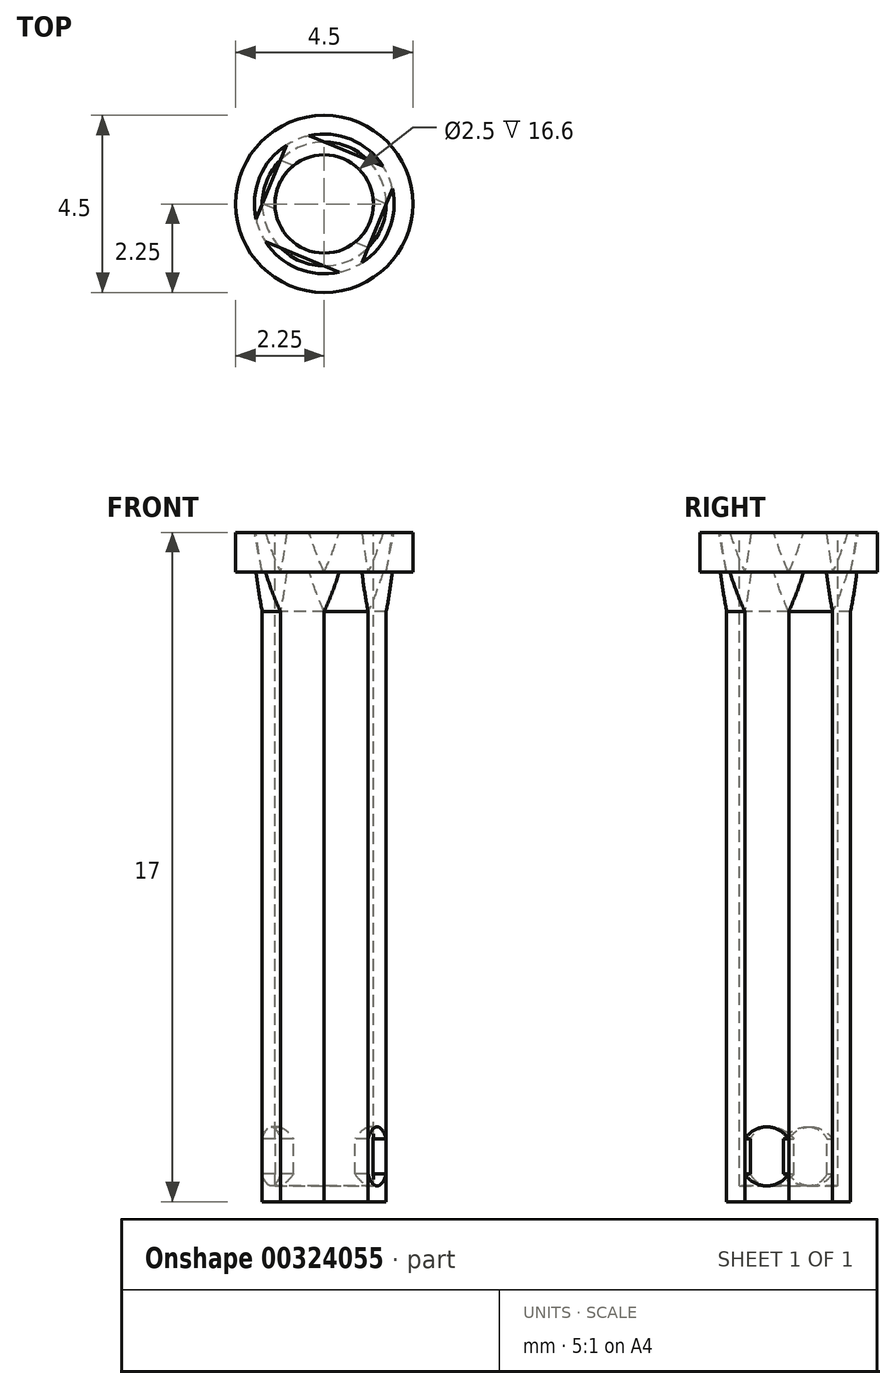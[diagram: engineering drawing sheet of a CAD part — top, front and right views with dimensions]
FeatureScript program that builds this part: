
annotation { "Feature Type Name" : "Feature", "Feature Type Description" : "" }
export const myFeature = defineFeature(function(context is Context, id is Id, definition is map)
    precondition{}
    {
        {
            var Q0;
            Q0=qCreatedBy(makeId("Front.planeOp"),FACE);
            var sketch = newSketch(context, id + "F0", { "sketchPlane" : qUnion([Q0])});
            skLineSegment(sketch, "E0.bottom", {"start": v(0, 0) * mm, "end": v(-1.58, 0) * mm});
            skLineSegment(sketch, "E0.top", {"start": v(0, 17) * mm, "end": v(-1.58, 17) * mm});
            skLineSegment(sketch, "E0.left", {"start": v(0, 0) * mm, "end": v(0, 17) * mm});
            skLineSegment(sketch, "E0.right", {"start": v(-1.58, 0) * mm, "end": v(-1.58, 17) * mm});
            skLineSegment(sketch, "E1.bottom", {"start": v(-1.58, 17) * mm, "end": v(-2.25, 17) * mm});
            skLineSegment(sketch, "E1.top", {"start": v(-1.58, 16) * mm, "end": v(-2.25, 16) * mm});
            skLineSegment(sketch, "E1.left", {"start": v(-1.58, 17) * mm, "end": v(-1.58, 16) * mm});
            skLineSegment(sketch, "E1.right", {"start": v(-2.25, 17) * mm, "end": v(-2.25, 16) * mm});
            skLineSegment(sketch, "E2.bottom", {"start": v(-1.25, 17) * mm, "end": v(0, 17) * mm});
            skLineSegment(sketch, "E2.top", {"start": v(-1.25, 0.4) * mm, "end": v(0, 0.4) * mm});
            skLineSegment(sketch, "E2.left", {"start": v(-1.25, 17) * mm, "end": v(-1.25, 0.4) * mm});
            skLineSegment(sketch, "E2.right", {"start": v(0, 17) * mm, "end": v(0, 0.4) * mm});
            skSolve(sketch);
        }
        {
            var Q0;
            Q0=makeQuery(id+"F0.imprint","IMPRINT",FACE,{"disambiguationData":[TD([[makeQuery(id+"F0.imprint","IMPRINT",EDGE,{"derivedFrom":sQuery(id+"F0.wireOp",EDGE,"E0.bottom")}),-1.0]])]});
            var Q1;
            Q1=makeQuery(id+"F0.imprint","IMPRINT",FACE,{"disambiguationData":[TD([[makeQuery(id+"F0.imprint","IMPRINT",EDGE,{"derivedFrom":sQuery(id+"F0.wireOp",EDGE,"E1.bottom")}),1.0]])]});
            var Q2;
            Q2=sQuery(id+"F0.wireOp",EDGE,"E2.right");
            revolve(context, id + "F1", {"entities" : qUnion([Q0, Q1]), "axis" : qUnion([Q2]), "revolveType" : RevolveType.FULL});
        }
        {
            var Q0;
            Q0=makeQuery(id+"F1.opRevolve","SWEPT_FACE",FACE,{"disambiguationData":[OSD([sQuery(id+"F0.wireOp",EDGE,"E0.bottom")])]});
            var sketch = newSketch(context, id + "F2", { "sketchPlane" : qUnion([Q0])});
            skCircle(sketch, "E3.cCircle", {"center": v(0, 0) * mm, "radius": 1.46 * mm, "construction": true});
            skLineSegment(sketch, "E3.0", {"start": v(1.11, -1.11) * mm, "end": v(0, -1.58) * mm});
            skLineSegment(sketch, "E3.1", {"start": v(0, -1.58) * mm, "end": v(-1.11, -1.11) * mm});
            skLineSegment(sketch, "E3.2", {"start": v(-1.11, -1.11) * mm, "end": v(-1.58, 0) * mm});
            skLineSegment(sketch, "E3.3", {"start": v(-1.58, 0) * mm, "end": v(-1.11, 1.11) * mm});
            skLineSegment(sketch, "E3.4", {"start": v(-1.11, 1.11) * mm, "end": v(0, 1.58) * mm});
            skLineSegment(sketch, "E3.5", {"start": v(0, 1.58) * mm, "end": v(1.11, 1.11) * mm});
            skLineSegment(sketch, "E3.6", {"start": v(1.11, 1.11) * mm, "end": v(1.58, 0) * mm});
            skLineSegment(sketch, "E3.7", {"start": v(1.58, 0) * mm, "end": v(1.11, -1.11) * mm});
            skPoint(sketch, "E3.0.midPoint", {"position": v(0.56, -1.34) * mm});
            skCircle(sketch, "E4", {"center": v(0, 0) * mm, "radius": 1.58 * mm});
            skSolve(sketch);
        }
        {
            var Q0;
            {var subQ0=sQuery(id+"F2.wireOp",EDGE,"E3.2");Q0=makeQuery(id+"F2.imprint","IMPRINT",FACE,{"disambiguationData":[TD([[makeQuery(id+"F2.imprint","IMPRINT",EDGE,{"derivedFrom":subQ0}),1.0]])]});}
            var Q1;
            {var subQ0=sQuery(id+"F2.wireOp",EDGE,"E3.4");Q1=makeQuery(id+"F2.imprint","IMPRINT",FACE,{"disambiguationData":[TD([[makeQuery(id+"F2.imprint","IMPRINT",EDGE,{"derivedFrom":subQ0}),1.0]])]});}
            var Q2;
            {var subQ0=sQuery(id+"F2.wireOp",EDGE,"E3.6");Q2=makeQuery(id+"F2.imprint","IMPRINT",FACE,{"disambiguationData":[TD([[makeQuery(id+"F2.imprint","IMPRINT",EDGE,{"derivedFrom":subQ0}),1.0]])]});}
            var Q3;
            {var subQ0=sQuery(id+"F2.wireOp",EDGE,"E3.0");Q3=makeQuery(id+"F2.imprint","IMPRINT",FACE,{"disambiguationData":[TD([[makeQuery(id+"F2.imprint","IMPRINT",EDGE,{"derivedFrom":subQ0}),1.0]])]});}
            extrude(context, id + "F3", {"entities" : qUnion([Q0, Q1, Q2, Q3]), "operationType" : NewBodyOperationType.REMOVE, "endBound" : BoundingType.THROUGH_ALL, "oppositeDirection" : true, "depth" : 25 * mm});
        }
        {
            var Q0;
            {var subQ0=sQuery(id+"F0.wireOp",EDGE,"E1.top");var subQ1=sQuery(id+"F2.wireOp",EDGE,"E4");var subQ2=sQuery(id+"F2.wireOp",EDGE,"E3.2");Q0=makeQuery(id+"F3.boolean.opBoolean","SPLIT",EDGE,{"disambiguationData":[topologyDisambiguationEdgeConnected([makeQuery(id+"F1.opRevolve","SWEPT_FACE",FACE,{"disambiguationData":[OSD([subQ0])]}),makeQuery(id+"F3.opExtrude","SWEPT_FACE",FACE,{"disambiguationData":[OSD([subQ1]),TDD([makeQuery(id+"F2.imprint","IMPRINT",EDGE,{"disambiguationData":[TD([[makeQuery(id+"F2.imprint","INTERSECT",VERTEX,{"derivedFrom":[sQuery(id+"F2.wireOp",EDGE,"E3.1"),subQ2,subQ1]}),-1.0]])],"derivedFrom":subQ1})])]})])],"derivedFrom":makeQuery(id+"F1.opRevolve","SWEPT_EDGE",EDGE,{"disambiguationData":[OSD([sQuery(id+"F0.wireOp",EDGE,"E0.right"),subQ0,sQuery(id+"F0.wireOp",EDGE,"E1.left")])]})});}
            var Q1;
            {var subQ0=sQuery(id+"F0.wireOp",EDGE,"E1.top");var subQ1=sQuery(id+"F2.wireOp",EDGE,"E4");var subQ2=sQuery(id+"F2.wireOp",EDGE,"E3.4");Q1=makeQuery(id+"F3.boolean.opBoolean","SPLIT",EDGE,{"disambiguationData":[topologyDisambiguationEdgeConnected([makeQuery(id+"F1.opRevolve","SWEPT_FACE",FACE,{"disambiguationData":[OSD([subQ0])]}),makeQuery(id+"F3.opExtrude","SWEPT_FACE",FACE,{"disambiguationData":[OSD([subQ1]),TDD([makeQuery(id+"F2.imprint","IMPRINT",EDGE,{"disambiguationData":[TD([[makeQuery(id+"F2.imprint","INTERSECT",VERTEX,{"derivedFrom":[sQuery(id+"F2.wireOp",EDGE,"E3.3"),subQ2,subQ1]}),-1.0]])],"derivedFrom":subQ1})])]})])],"derivedFrom":makeQuery(id+"F1.opRevolve","SWEPT_EDGE",EDGE,{"disambiguationData":[OSD([sQuery(id+"F0.wireOp",EDGE,"E0.right"),subQ0,sQuery(id+"F0.wireOp",EDGE,"E1.left")])]})});}
            var Q2;
            {var subQ0=sQuery(id+"F0.wireOp",EDGE,"E1.top");var subQ1=sQuery(id+"F2.wireOp",EDGE,"E4");var subQ2=sQuery(id+"F2.wireOp",EDGE,"E3.6");Q2=makeQuery(id+"F3.boolean.opBoolean","SPLIT",EDGE,{"disambiguationData":[topologyDisambiguationEdgeConnected([makeQuery(id+"F1.opRevolve","SWEPT_FACE",FACE,{"disambiguationData":[OSD([subQ0])]}),makeQuery(id+"F3.opExtrude","SWEPT_FACE",FACE,{"disambiguationData":[OSD([subQ1]),TDD([makeQuery(id+"F2.imprint","IMPRINT",EDGE,{"disambiguationData":[TD([[makeQuery(id+"F2.imprint","INTERSECT",VERTEX,{"derivedFrom":[sQuery(id+"F2.wireOp",EDGE,"E3.5"),subQ2,subQ1]}),-1.0]])],"derivedFrom":subQ1})])]})])],"derivedFrom":makeQuery(id+"F1.opRevolve","SWEPT_EDGE",EDGE,{"disambiguationData":[OSD([sQuery(id+"F0.wireOp",EDGE,"E0.right"),subQ0,sQuery(id+"F0.wireOp",EDGE,"E1.left")])]})});}
            var Q3;
            {var subQ0=sQuery(id+"F0.wireOp",EDGE,"E1.top");var subQ1=sQuery(id+"F2.wireOp",EDGE,"E4");var subQ2=sQuery(id+"F2.wireOp",EDGE,"E3.0");Q3=makeQuery(id+"F3.boolean.opBoolean","SPLIT",EDGE,{"disambiguationData":[topologyDisambiguationEdgeConnected([makeQuery(id+"F1.opRevolve","SWEPT_FACE",FACE,{"disambiguationData":[OSD([subQ0])]}),makeQuery(id+"F3.opExtrude","SWEPT_FACE",FACE,{"disambiguationData":[OSD([subQ1]),TDD([makeQuery(id+"F2.imprint","IMPRINT",EDGE,{"disambiguationData":[TD([[makeQuery(id+"F2.imprint","INTERSECT",VERTEX,{"derivedFrom":[subQ2,sQuery(id+"F2.wireOp",EDGE,"E3.7"),subQ1]}),-1.0]])],"derivedFrom":subQ1})])]})])],"derivedFrom":makeQuery(id+"F1.opRevolve","SWEPT_EDGE",EDGE,{"disambiguationData":[OSD([sQuery(id+"F0.wireOp",EDGE,"E0.right"),subQ0,sQuery(id+"F0.wireOp",EDGE,"E1.left")])]})});}
            var Q4;
            {var subQ0=sQuery(id+"F2.wireOp",EDGE,"E4");var subQ1=sQuery(id+"F2.wireOp",EDGE,"E3.0");Q4=makeQuery(id+"F3.boolean.opBoolean","INTERSECT",EDGE,{"derivedFrom":[makeQuery(id+"F1.opRevolve","SWEPT_FACE",FACE,{"disambiguationData":[OSD([sQuery(id+"F0.wireOp",EDGE,"E0.top"),sQuery(id+"F0.wireOp",EDGE,"E1.bottom")])]}),makeQuery(id+"F3.opExtrude","SWEPT_FACE",FACE,{"disambiguationData":[OSD([subQ0]),TDD([makeQuery(id+"F2.imprint","IMPRINT",EDGE,{"disambiguationData":[TD([[makeQuery(id+"F2.imprint","INTERSECT",VERTEX,{"derivedFrom":[subQ1,sQuery(id+"F2.wireOp",EDGE,"E3.7"),subQ0]}),-1.0]])],"derivedFrom":subQ0})])]})]});}
            var Q5;
            {var subQ0=sQuery(id+"F2.wireOp",EDGE,"E4");var subQ1=sQuery(id+"F2.wireOp",EDGE,"E3.2");Q5=makeQuery(id+"F3.boolean.opBoolean","INTERSECT",EDGE,{"derivedFrom":[makeQuery(id+"F1.opRevolve","SWEPT_FACE",FACE,{"disambiguationData":[OSD([sQuery(id+"F0.wireOp",EDGE,"E0.top"),sQuery(id+"F0.wireOp",EDGE,"E1.bottom")])]}),makeQuery(id+"F3.opExtrude","SWEPT_FACE",FACE,{"disambiguationData":[OSD([subQ0]),TDD([makeQuery(id+"F2.imprint","IMPRINT",EDGE,{"disambiguationData":[TD([[makeQuery(id+"F2.imprint","INTERSECT",VERTEX,{"derivedFrom":[sQuery(id+"F2.wireOp",EDGE,"E3.1"),subQ1,subQ0]}),-1.0]])],"derivedFrom":subQ0})])]})]});}
            var Q6;
            {var subQ0=sQuery(id+"F2.wireOp",EDGE,"E4");var subQ1=sQuery(id+"F2.wireOp",EDGE,"E3.4");Q6=makeQuery(id+"F3.boolean.opBoolean","INTERSECT",EDGE,{"derivedFrom":[makeQuery(id+"F1.opRevolve","SWEPT_FACE",FACE,{"disambiguationData":[OSD([sQuery(id+"F0.wireOp",EDGE,"E0.top"),sQuery(id+"F0.wireOp",EDGE,"E1.bottom")])]}),makeQuery(id+"F3.opExtrude","SWEPT_FACE",FACE,{"disambiguationData":[OSD([subQ0]),TDD([makeQuery(id+"F2.imprint","IMPRINT",EDGE,{"disambiguationData":[TD([[makeQuery(id+"F2.imprint","INTERSECT",VERTEX,{"derivedFrom":[sQuery(id+"F2.wireOp",EDGE,"E3.3"),subQ1,subQ0]}),-1.0]])],"derivedFrom":subQ0})])]})]});}
            var Q7;
            {var subQ0=sQuery(id+"F2.wireOp",EDGE,"E4");var subQ1=sQuery(id+"F2.wireOp",EDGE,"E3.6");Q7=makeQuery(id+"F3.boolean.opBoolean","INTERSECT",EDGE,{"derivedFrom":[makeQuery(id+"F1.opRevolve","SWEPT_FACE",FACE,{"disambiguationData":[OSD([sQuery(id+"F0.wireOp",EDGE,"E0.top"),sQuery(id+"F0.wireOp",EDGE,"E1.bottom")])]}),makeQuery(id+"F3.opExtrude","SWEPT_FACE",FACE,{"disambiguationData":[OSD([subQ0]),TDD([makeQuery(id+"F2.imprint","IMPRINT",EDGE,{"disambiguationData":[TD([[makeQuery(id+"F2.imprint","INTERSECT",VERTEX,{"derivedFrom":[sQuery(id+"F2.wireOp",EDGE,"E3.5"),subQ1,subQ0]}),-1.0]])],"derivedFrom":subQ0})])]})]});}
            chamfer(context, id + "F4", {"entities" : qUnion([Q0, Q1, Q2, Q3, Q4, Q5, Q6, Q7]), "chamferType" : ChamferType.TWO_OFFSETS, "width1" : .2 * mm, "oppositeDirection" : false, "width2" : 1 * mm, "tangentPropagation" : true});
        }
        {
            var Q0;
            Q0=makeQuery(id+"F3.boolean.opBoolean","COPY",FACE,{"derivedFrom":makeQuery(id+"F3.opExtrude","SWEPT_FACE",FACE,{"disambiguationData":[OSD([sQuery(id+"F2.wireOp",EDGE,"E3.2")])]})});
            var sketch = newSketch(context, id + "F5", { "sketchPlane" : qUnion([Q0])});
            skCircle(sketch, "E5", {"center": v(0, 1.15) * mm, "radius": 0.75 * mm});
            skPoint(sketch, "E5.centerSnap0", {"position": v(0, 0) * mm});
            skLineSegment(sketch, "E6.0", {"start": v(-1.25, 0.4) * mm, "end": v(1.25, 0.4) * mm});
            skSolve(sketch);
        }
        {
            var Q0;
            {var subQ0=sQuery(id+"F5.wireOp",EDGE,"E5");var subQ8=makeQuery(id+"F5.imprint","INTERSECT",VERTEX,{"derivedFrom":[subQ0,sQuery(id+"F5.wireOp",EDGE,"E6.0")]});Q0=makeQuery(id+"F5.imprint","IMPRINT",FACE,{"disambiguationData":[TD([[makeQuery(id+"F5.imprint","IMPRINT",EDGE,{"disambiguationData":[TD([[subQ8,1.0]])],"derivedFrom":subQ0}),1.0]])]});}
            var Q1;
            {var subQ0=sQuery(id+"F5.wireOp",EDGE,"E5");var subQ1=sQuery(id+"F2.wireOp",EDGE,"E3.2");var subQ2=makeQuery(id+"F3.boolean.opBoolean","COPY",EDGE,{"disambiguationData":[topologyDisambiguationEdgeConnected([makeQuery(id+"F1.opRevolve","SWEPT_FACE",FACE,{"disambiguationData":[OSD([sQuery(id+"F0.wireOp",EDGE,"E0.right")])]})])],"derivedFrom":makeQuery(id+"F3.opExtrude","SWEPT_EDGE",EDGE,{"disambiguationData":[OSD([subQ1,sQuery(id+"F2.wireOp",EDGE,"E3.3"),sQuery(id+"F2.wireOp",EDGE,"E4")])]})});var subQ3=makeQuery(id+"F5.imprint","INTERSECT",VERTEX,{"disambiguationData":[OD(0.0)],"derivedFrom":[subQ2,subQ0]});Q1=makeQuery(id+"F5.imprint","IMPRINT",FACE,{"disambiguationData":[TD([[makeQuery(id+"F5.imprint","IMPRINT",EDGE,{"disambiguationData":[TD([[subQ3,1.0]])],"derivedFrom":subQ0}),1.0]])]});}
            var Q2;
            {var subQ0=sQuery(id+"F5.wireOp",EDGE,"E5");var subQ1=sQuery(id+"F2.wireOp",EDGE,"E3.2");var subQ2=makeQuery(id+"F3.boolean.opBoolean","COPY",EDGE,{"disambiguationData":[topologyDisambiguationEdgeConnected([makeQuery(id+"F1.opRevolve","SWEPT_FACE",FACE,{"disambiguationData":[OSD([sQuery(id+"F0.wireOp",EDGE,"E0.right")])]})])],"derivedFrom":makeQuery(id+"F3.opExtrude","SWEPT_EDGE",EDGE,{"disambiguationData":[OSD([sQuery(id+"F2.wireOp",EDGE,"E3.1"),subQ1,sQuery(id+"F2.wireOp",EDGE,"E4")])]})});var subQ3=makeQuery(id+"F5.imprint","INTERSECT",VERTEX,{"disambiguationData":[OD(0.0)],"derivedFrom":[subQ2,subQ0]});Q2=makeQuery(id+"F5.imprint","IMPRINT",FACE,{"disambiguationData":[TD([[makeQuery(id+"F5.imprint","IMPRINT",EDGE,{"disambiguationData":[TD([[subQ3,-1.0]])],"derivedFrom":subQ0}),1.0]])]});}
            extrude(context, id + "F6", {"entities" : qUnion([Q0, Q1, Q2]), "operationType" : NewBodyOperationType.REMOVE, "oppositeDirection" : true, "depth" : 25 * mm, "offsetDistance" : 25 * mm});
        }
    });
